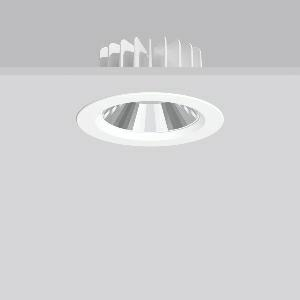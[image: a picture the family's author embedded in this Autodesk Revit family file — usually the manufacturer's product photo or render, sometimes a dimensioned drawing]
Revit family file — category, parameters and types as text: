
# Revit family: ledona_round_ip20_901795_002_1_76_30fa
name_source: partatom
category: Lighting Fixtures
units: mm (PartAtom-declared; Revit-internal decimal feet)

## family parameters
Cut with Voids When Loaded = No
Host = Face
Light Source = No
Part Type = Normal
Room Calculation Point = No
Round Connector Dimension = Use Diameter
Shared = No

## types (1)
- MultiLumen 1 (1 x LED Modul 940, 1700 lm, 4000)
    Apparent Load = 12 VA
    Approval mark = CE
    CIE Flux Codes = 91 100 100 100 100
    Color Rendering = 92
    Color Temperature = 4000
    Default Elevation = 1800 mm
    Description = Series: LEDONA round
Recessed LED downlight featuring advanced technology and sophisticated design. Housing: die-cast aluminium constructed as heat sink.Bezel ring: die-cast aluminium, powder-coated. Open version. Highly polished four-segment faceted aluminium reflector with light mixing chamber. MultiLumen: Luminous flux adjustable in different steps. Best colour rendering index Ra>90. Installation without tools thanks to spring fastening system. Connected converter included in separate gearbox. With connecting cable (L 250 mm). Suitable for through wiring as standard. 
Colour: white
Diameter: 180 mm
Height: 3 mm
Cut-out diameter: 160 mm
Recess height: 89 mm
Luminaire: recess height: 89 mm
Lamp: LED
Socket: without socket
Colour temperature: 4000K
Colour rendering index (CRI): 92
System power: 12 W
Rated luminous flux: 1700 lm
Luminous efficiency: 142 lm/W
System power 2: 19 W
Rated luminous flux 2: 2750 lm
Luminous efficiency 2: 145 lm/W
System power 3: 27 W
Rated luminous flux 3: 3700 lm
Luminous efficiency 3: 137 lm/W
System power 4: 39 W
Rated luminous flux 4: 4950 lm
Luminous efficiency 4: 127 lm/W
Control gear: Converter, dimmable, DALI
Protection class: II
Type of protection: IP 20
    Height = 0 mm  [stored 0 ft]
    Lamp = 1 x LED Modul 940
    Lamp Light Flux = 1700 lm
    Lamp count = 1
    Length = 180 mm  [stored 0.590551 ft]
    Lifetime = 50000 h
    Luminous efficacy = 142 lm/W
    Manufacturer = RZB
    ModVariant = No
    Model = 901795.002.1.76
    Mounting Place = Ceiling
    Mounting Type = Recessed
    Number of Poles = 1
    OnlyDefault = Yes
    Power Factor = 1
    Product Name = LEDONA round IP20
    Product group = Recessed downlights
    ProductGroupID = 402
    Protection Class = Protection class II
    Protection Degree = IP 20
    RLX_Detail_Level = 1
    RLX_Emergency_Light_Flux = 0 lm
    RLX_Emergency_Type = 0
    RLX_Emergency_Type_DB = No
    RlxData = <blob elided: 38073 chars, md5=915e0feb>
    Socket = socket
    Standby Power = 0 W
    System Light Flux = 1700 lm
    System Power = 12 W
    Type Comments = MultiLumen 1
    Type Image = 901385.002.jpg
    URL = http://relux.com
    VarID = multilumen_1
    Voltage = 230 V
    Voltage Range = 220-240 V
    Weight = 0.00 kg
    Width = 0 mm  [stored 0 ft]

note: [stored X ft] marks values corroborated as IEEE doubles in the binary element streams (Revit-internal decimal feet)

## geometry (parser evidence)
native form markers: Blend x4, Sweep x11
no freeform markers — native parametric forms only
